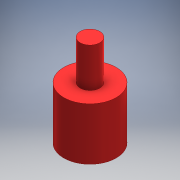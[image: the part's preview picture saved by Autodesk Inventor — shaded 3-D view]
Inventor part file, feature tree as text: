
AUTODESK INVENTOR PART (.ipt)
format: ipt  version: 2016 (Build 200138000, 138)  size: 104,448 bytes
history: native  units: mm
features: other x2, sketch x2, extrude x2, hole x1
ambient origin geometry x8: Origin, YZ Plane, XZ Plane, XY Plane, X Axis, Y Axis, Z Axis, Center Point
bodies: Body1 (feature_tree)
feature tree (7):
  other  "ソリッド1"
  sketch  "スケッチ1"
  extrude  "押し出し1"  Depth=8.0mm
  extrude  "押し出し2"  Depth=3.0mm
  hole  "穴1"  [1 undecoded]
  sketch  "スケッチ2"
  other  "断面エッジを投影1"
note: 1 required parameter value undecoded (feature->parameter linkage not recoverable at this tier; creation-order binding heuristic only, values carry confidence <= 0.55)
